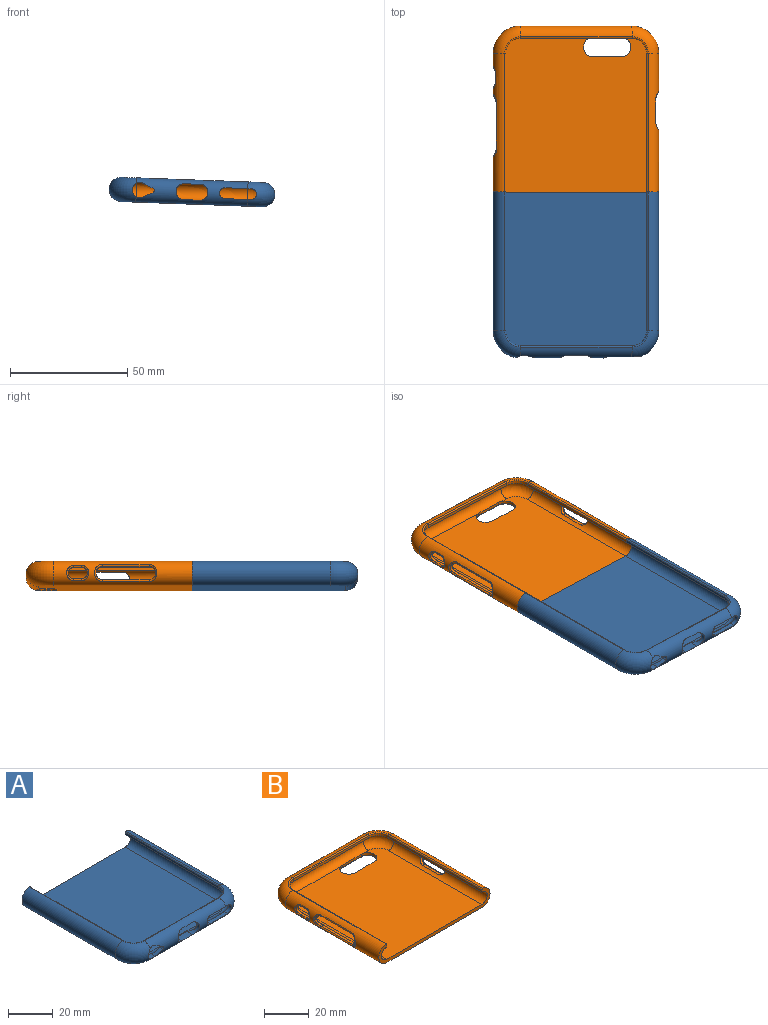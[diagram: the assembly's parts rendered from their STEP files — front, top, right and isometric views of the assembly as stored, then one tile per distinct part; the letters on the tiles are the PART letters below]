
ASSEMBLY  parts=2 mates=3
PART A: 35 faces, bbox 72.6x71.8x10.4 mm
  f0: plane 47.52x1.24mm, normal (0,1,0), area 59mm2, adj f13,f14,f16,f18
  f1: cylinder r=2.32mm len=4.65mm, axis (0,1,0), area 14.2mm2, adj f10,f12,f14,f20
  f2: plane 4.25x3.36mm, normal (-0.43,0,0.9), area 9.7mm2, adj f3,f5,f14,f20
  f3: cylinder r=1mm len=1.9mm, axis (0,1,0), area 4mm2, adj f2,f4,f14,f20
  f4: plane 4.25x3.35mm, normal (-0.43,0,-0.9), area 9.7mm2, adj f3,f5,f14,f20
  f5: cylinder r=3.25mm len=6.5mm, axis (0,1,0), area 31.1mm2, adj f2,f4,f14,f17,f19,f20
  f6: cylinder r=3.4mm len=6.8mm, axis (0,1,0), area 25.3mm2, adj f7,f9,f14,f20
  f7: plane 6.85x3.56mm, normal (0,0,1), area 24.4mm2, adj f6,f8,f14,f20
  f8: cylinder r=3.4mm len=6.8mm, axis (0,1,0), area 25.3mm2, adj f7,f9,f14,f20
  f9: plane 6.85x3.49mm, normal (0,0,-1), area 23.9mm2, adj f6,f8,f14,f20
  f10: plane 11.25x2.27mm, normal (0,0,1), area 24.1mm2, adj f1,f11,f14,f15,f20,f21
  f11: cylinder r=2.32mm len=4.65mm, axis (0,1,0), area 14.8mm2, adj f10,f12,f15,f21
  f12: plane 11.25x2.26mm, normal (0,0,-1), area 24.1mm2, adj f1,f11,f14,f15,f20,f21
  f13: cylinder r=0.51mm len=47.52mm, axis (-1,0,0), area 40.5mm2, adj f0,f20,f22,f23
  f14: cylinder r=3.43mm len=47.52mm, axis (-1,0,0), area 297mm2, adj f0,f1,f2,f3,f4,f5,f6,f7
  f15: torus R=6.37mm, axis (0,0,-1), area 127.5mm2, adj f10,f11,f12,f14,f16,f32,f33
  f16: cylinder r=6.37mm len=6.37mm, axis (0,0,-1), area 12.4mm2, adj f0,f15,f22,f31
  f17: torus R=6.37mm, axis (0,0,-1), area 136.6mm2, adj f5,f14,f18,f30,f33
  f18: cylinder r=6.37mm len=6.37mm, axis (0,0,-1), area 12.4mm2, adj f0,f17,f23,f29
  f19: torus R=6.37mm, axis (0,0,-1), area 235.3mm2, adj f5,f20,f23,f25,f26
  f20: cylinder r=5.2mm len=47.52mm, axis (-1,0,0), area 567.6mm2, adj f1,f2,f3,f4,f5,f6,f7,f8
  f21: torus R=6.37mm, axis (0,0,-1), area 226.6mm2, adj f10,f11,f12,f20,f22,f25,f28
  f22: torus R=6.88mm, axis (0,0,1), area 8.8mm2, adj f13,f16,f21,f27
  f23: torus R=6.88mm, axis (0,0,1), area 8.8mm2, adj f13,f18,f19,f24
  f24: cylinder r=0.51mm len=59.27mm, axis (0,1,0), area 50.6mm2, adj f23,f26,f29,f34
  f25: plane 65.64x60.26mm, normal (0,0,-1), area 3938.2mm2, adj f19,f20,f21,f26,f28,f34
  f26: cylinder r=5.2mm len=59.27mm, axis (0,1,0), area 935.4mm2, adj f19,f24,f25,f34
  f27: cylinder r=0.51mm len=59.27mm, axis (0,-1,0), area 50.6mm2, adj f22,f28,f31,f34
  f28: cylinder r=5.2mm len=59.27mm, axis (0,-1,0), area 935.4mm2, adj f21,f25,f27,f34
  f29: plane 59.27x1.24mm, normal (1,0,0), area 73.6mm2, adj f18,f24,f30,f34
  f30: cylinder r=3.43mm len=59.27mm, axis (0,1,0), area 637.7mm2, adj f17,f29,f33,f34
  f31: plane 59.27x1.24mm, normal (-1,0,0), area 73.6mm2, adj f16,f27,f32,f34
  f32: cylinder r=3.43mm len=59.27mm, axis (0,-1,0), area 637.7mm2, adj f15,f31,f33,f34
  f33: plane 65.64x60.26mm, normal (0,0,1), area 3938.2mm2, adj f14,f15,f17,f30,f32,f34
  f34: plane 70.67x10.38mm, normal (0,1,0), area 155.2mm2, adj f24,f25,f26,f27,f28,f29,f30,f31
PART B: 57 faces, bbox 72.6x71.8x10.4 mm
  f0: plane 65.64x60.26mm, normal (0,0,1), area 3790.2mm2, adj f1,f3,f10,f11,f14,f19,f20,f21
  f1: cylinder r=3.43mm len=59.27mm, axis (0,-1,0), area 543.7mm2, adj f0,f2,f11,f40,f41,f42,f43,f56
  f2: plane 59.27x1.24mm, normal (-1,0,0), area 73.6mm2, adj f1,f8,f12,f56
  f3: cylinder r=3.43mm len=59.27mm, axis (0,1,0), area 440.9mm2, adj f0,f4,f14,f32,f33,f34,f35,f36
  f4: plane 59.27x1.24mm, normal (1,0,0), area 73.6mm2, adj f3,f9,f15,f56
  f5: cylinder r=5.2mm len=59.27mm, axis (0,-1,0), area 811.7mm2, adj f7,f8,f16,f44,f45,f46,f47,f56
  f6: cylinder r=5.2mm len=59.27mm, axis (0,1,0), area 675.9mm2, adj f7,f9,f18,f48,f49,f50,f51,f52
  f7: plane 65.64x60.26mm, normal (0,0,-1), area 3772.3mm2, adj f5,f6,f16,f17,f18,f23,f24,f25
  f8: cylinder r=0.51mm len=59.27mm, axis (0,-1,0), area 50.6mm2, adj f2,f5,f29,f56
  f9: cylinder r=0.51mm len=59.27mm, axis (0,1,0), area 50.6mm2, adj f4,f6,f31,f56
  f10: cylinder r=3.43mm len=47.52mm, axis (1,0,0), area 507.7mm2, adj f0,f11,f13,f14,f19,f21,f22
  f11: torus R=6.37mm, axis (0,0,-1), area 144.5mm2, adj f0,f1,f10,f12
  f12: cylinder r=6.37mm len=6.37mm, axis (0,0,-1), area 12.4mm2, adj f2,f11,f13,f29
  f13: plane 47.52x1.24mm, normal (0,-1,0), area 59mm2, adj f10,f12,f15,f30
  f14: torus R=6.37mm, axis (0,0,-1), area 144.5mm2, adj f0,f3,f10,f15
  f15: cylinder r=6.37mm len=6.37mm, axis (0,0,-1), area 12.4mm2, adj f4,f13,f14,f31
  f16: torus R=6.37mm, axis (0,0,-1), area 242.7mm2, adj f5,f7,f17,f29
  f17: cylinder r=5.2mm len=47.52mm, axis (1,0,0), area 736.7mm2, adj f7,f16,f18,f26,f27,f28,f30
  f18: torus R=6.37mm, axis (0,0,-1), area 242.7mm2, adj f6,f7,f17,f31
  f19: cylinder r=4.1mm len=8.2mm, axis (0,0,1), area 16.3mm2, adj f0,f10,f20,f22,f25,f27
  f20: plane 12.06x1.27mm, normal (0,1,0), area 15.3mm2, adj f0,f19,f21,f23
  f21: cylinder r=4.1mm len=8.2mm, axis (0,0,1), area 16.3mm2, adj f0,f10,f20,f22,f24,f26
  f22: plane 12.06x1.22mm, normal (0,-1,0), area 14.7mm2, adj f10,f19,f21,f28
  f23: cylinder r=0.51mm len=12.06mm, axis (1,0,0), area 9.6mm2, adj f7,f20,f24,f25
  f24: torus R=4.61mm, axis (0,0,-1), area 8.7mm2, adj f7,f21,f23,f26
  f25: torus R=4.61mm, axis (0,0,-1), area 8.7mm2, adj f7,f19,f23,f27
  f26: bspline ~4.26x1.79mm, area 2.1mm2, adj f17,f21,f24,f28
  f27: bspline ~4.26x1.79mm, area 2.1mm2, adj f17,f19,f25,f28
  f28: cylinder r=0.51mm len=12.06mm, axis (1,0,0), area 10.6mm2, adj f17,f22,f26,f27
  f29: torus R=6.88mm, axis (0,0,1), area 8.8mm2, adj f8,f12,f16,f30
  f30: cylinder r=0.51mm len=47.52mm, axis (1,0,0), area 40.5mm2, adj f13,f17,f29,f31
  f31: torus R=6.88mm, axis (0,0,1), area 8.8mm2, adj f9,f15,f18,f30
  f32: plane 3.63x1.25mm, normal (0,0,-1), area 4.5mm2, adj f3,f33,f35,f55
  f33: cylinder r=2.39mm len=4.77mm, axis (1,0,0), area 9.4mm2, adj f3,f32,f34,f53
  f34: plane 3.63x1.24mm, normal (0,0,1), area 4.5mm2, adj f3,f33,f35,f52
  f35: cylinder r=2.39mm len=4.77mm, axis (1,0,0), area 9.4mm2, adj f3,f32,f34,f54
  f36: plane 20.01x1.37mm, normal (0,0,-1), area 27.4mm2, adj f3,f37,f39,f51
  f37: cylinder r=2.8mm len=5.59mm, axis (1,0,0), area 11.4mm2, adj f3,f36,f38,f49
  f38: plane 20.01x1.35mm, normal (0,0,1), area 27mm2, adj f3,f37,f39,f48
  f39: cylinder r=2.8mm len=5.59mm, axis (1,0,0), area 11.4mm2, adj f3,f36,f38,f50
  f40: cylinder r=2.79mm len=5.59mm, axis (-1,0,0), area 11.4mm2, adj f1,f41,f43,f47
  f41: plane 10.2x1.37mm, normal (0,0,-1), area 13.9mm2, adj f1,f40,f42,f46
  f42: cylinder r=2.79mm len=5.59mm, axis (-1,0,0), area 11.4mm2, adj f1,f41,f43,f44
  f43: plane 10.2x1.35mm, normal (0,0,1), area 13.7mm2, adj f1,f40,f42,f45
  f44: bspline ~7.32x3.93mm, area 9.9mm2, adj f5,f42,f45,f46
  f45: cylinder r=0.51mm len=10.2mm, axis (0,-1,0), area 12.1mm2, adj f5,f43,f44,f47
  f46: cylinder r=0.51mm len=10.2mm, axis (0,-1,0), area 12.2mm2, adj f5,f41,f44,f47
  f47: bspline ~7.32x3.93mm, area 9.9mm2, adj f5,f40,f45,f46
  f48: cylinder r=0.51mm len=20.01mm, axis (0,1,0), area 23.8mm2, adj f6,f38,f49,f50
  f49: bspline ~7.33x3.94mm, area 9.9mm2, adj f6,f37,f48,f51
  f50: bspline ~7.33x3.93mm, area 9.9mm2, adj f6,f39,f48,f51
  f51: cylinder r=0.51mm len=20.01mm, axis (0,1,0), area 24mm2, adj f6,f36,f49,f50
  f52: cylinder r=0.51mm len=3.63mm, axis (0,1,0), area 4.1mm2, adj f6,f34,f53,f54
  f53: bspline ~6.42x3.47mm, area 8.2mm2, adj f6,f33,f52,f55
  f54: bspline ~6.42x3.47mm, area 8.2mm2, adj f6,f35,f52,f55
  f55: cylinder r=0.51mm len=3.63mm, axis (0,1,0), area 4.1mm2, adj f6,f32,f53,f54
  f56: plane 70.67x10.38mm, normal (0,-1,0), area 155.2mm2, adj f0,f1,f2,f3,f4,f5,f6,f7
PLACE A rot(axis=(0,1,0),2.1deg) t=(-1.57,6.58,-8.27)mm
PLACE B rot(axis=(0,1,0),2.1deg) t=(-1.57,6.58,-8.27)mm fixed
MATE planar B.f3 <-> A.f26  axis (0,-1,0) through (-31.5,6.58,-2.37)mm
MATE fastened B.f1 <-> A.f28  axis (0,-1,0) through (28.72,6.58,-4.59)mm
MATE cylindrical A.f26 <-> B.f3  axis (0,1,0) through (-31.5,6.58,-2.37)mm
